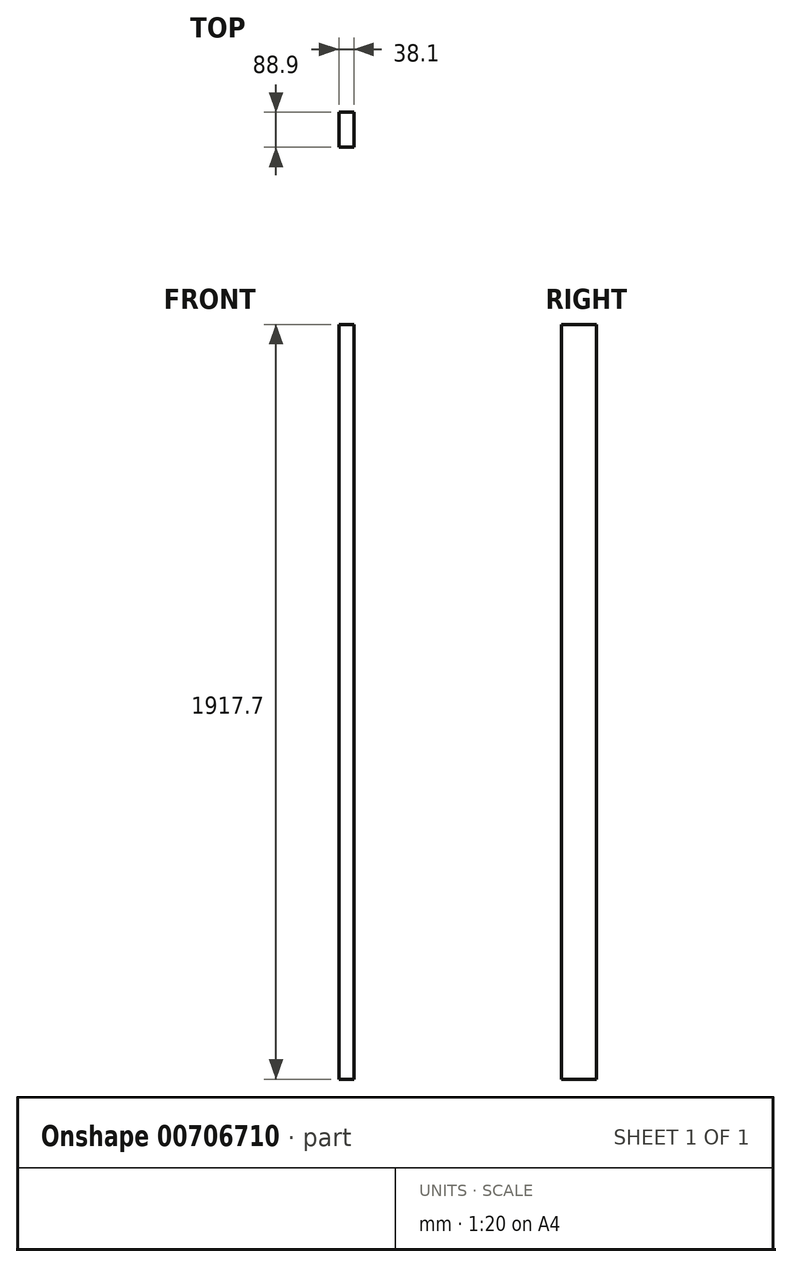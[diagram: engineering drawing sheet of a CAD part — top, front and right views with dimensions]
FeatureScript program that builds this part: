
annotation { "Feature Type Name" : "Feature", "Feature Type Description" : "" }
export const myFeature = defineFeature(function(context is Context, id is Id, definition is map)
    precondition{}
    {
        {
            var Q0;
            Q0=qCreatedBy(makeId("Front.planeOp"),FACE);
            var sketch = newSketch(context, id + "F0", { "sketchPlane" : qUnion([Q0])});
            skLineSegment(sketch, "E0.bottom", {"start": v(0, 0) * mm, "end": v(38.1, 0) * mm});
            skLineSegment(sketch, "E0.top", {"start": v(0, 1917.7) * mm, "end": v(38.1, 1917.7) * mm});
            skLineSegment(sketch, "E0.left", {"start": v(0, 0) * mm, "end": v(0, 1917.7) * mm});
            skLineSegment(sketch, "E0.right", {"start": v(38.1, 0) * mm, "end": v(38.1, 1917.7) * mm});
            skSolve(sketch);
        }
        {
            var Q0;
            Q0=makeQuery(id+"F0.imprint","IMPRINT",FACE,{"disambiguationData":[TD([[makeQuery(id+"F0.imprint","IMPRINT",EDGE,{"derivedFrom":sQuery(id+"F0.wireOp",EDGE,"E0.bottom")}),1.0]])]});
            extrude(context, id + "F1", {"entities" : qUnion([Q0]), "depth" : 88.9 * mm, "offsetDistance" : 25.4 * mm});
        }
    });
